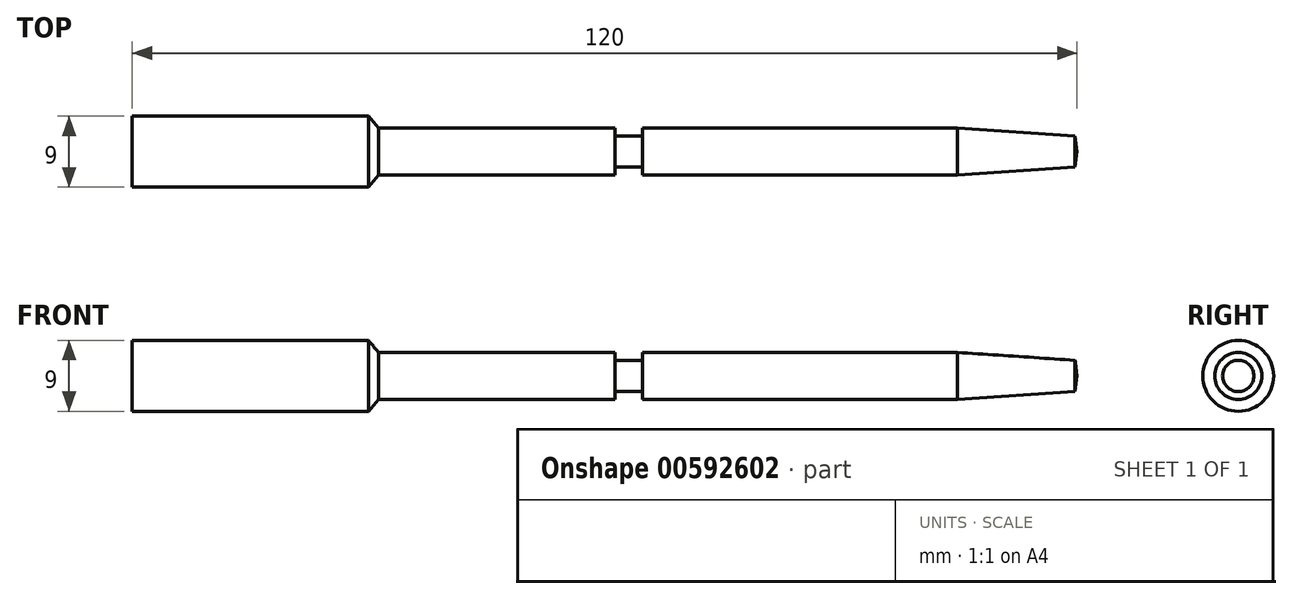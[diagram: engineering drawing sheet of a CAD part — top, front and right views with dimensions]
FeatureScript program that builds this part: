
annotation { "Feature Type Name" : "Feature", "Feature Type Description" : "" }
export const myFeature = defineFeature(function(context is Context, id is Id, definition is map)
    precondition{}
    {
        {
            var Q0;
            Q0=qCreatedBy(makeId("Front.planeOp"),FACE);
            var sketch = newSketch(context, id + "F0", { "sketchPlane" : qUnion([Q0])});
            skLineSegment(sketch, "E0", {"start": v(0, 0) * mm, "end": v(120, 0) * mm});
            skLineSegment(sketch, "E1", {"start": v(0, 0) * mm, "end": v(0, 4.5) * mm});
            skLineSegment(sketch, "E2", {"start": v(0, 4.5) * mm, "end": v(30, 4.5) * mm});
            skLineSegment(sketch, "E3", {"start": v(30, 4.5) * mm, "end": v(31.3, 2.99) * mm});
            skLineSegment(sketch, "E4", {"start": v(31.3, 2.99) * mm, "end": v(61.3, 2.99) * mm});
            skLineSegment(sketch, "E5", {"start": v(61.3, 2.99) * mm, "end": v(61.3, 1.99) * mm});
            skLineSegment(sketch, "E6", {"start": v(61.3, 1.99) * mm, "end": v(64.8, 1.99) * mm});
            skLineSegment(sketch, "E7", {"start": v(64.8, 1.99) * mm, "end": v(64.8, 2.99) * mm});
            skLineSegment(sketch, "E8", {"start": v(64.8, 2.99) * mm, "end": v(104.8, 2.99) * mm});
            skLineSegment(sketch, "E9", {"start": v(104.8, 2.99) * mm, "end": v(119.77, 1.99) * mm});
            skLineSegment(sketch, "E10", {"start": v(119.77, 1.99) * mm, "end": v(120, 0) * mm});
            skSolve(sketch);
        }
        {
            var Q0;
            Q0=makeQuery(id+"F0.imprint","IMPRINT",FACE,{"disambiguationData":[TD([[makeQuery(id+"F0.imprint","IMPRINT",EDGE,{"derivedFrom":sQuery(id+"F0.wireOp",EDGE,"E0")}),1.0]])]});
            var Q1;
            Q1=sQuery(id+"F0.wireOp",EDGE,"E0");
            revolve(context, id + "F1", {"entities" : qUnion([Q0]), "axis" : qUnion([Q1]), "revolveType" : RevolveType.FULL});
        }
    });
